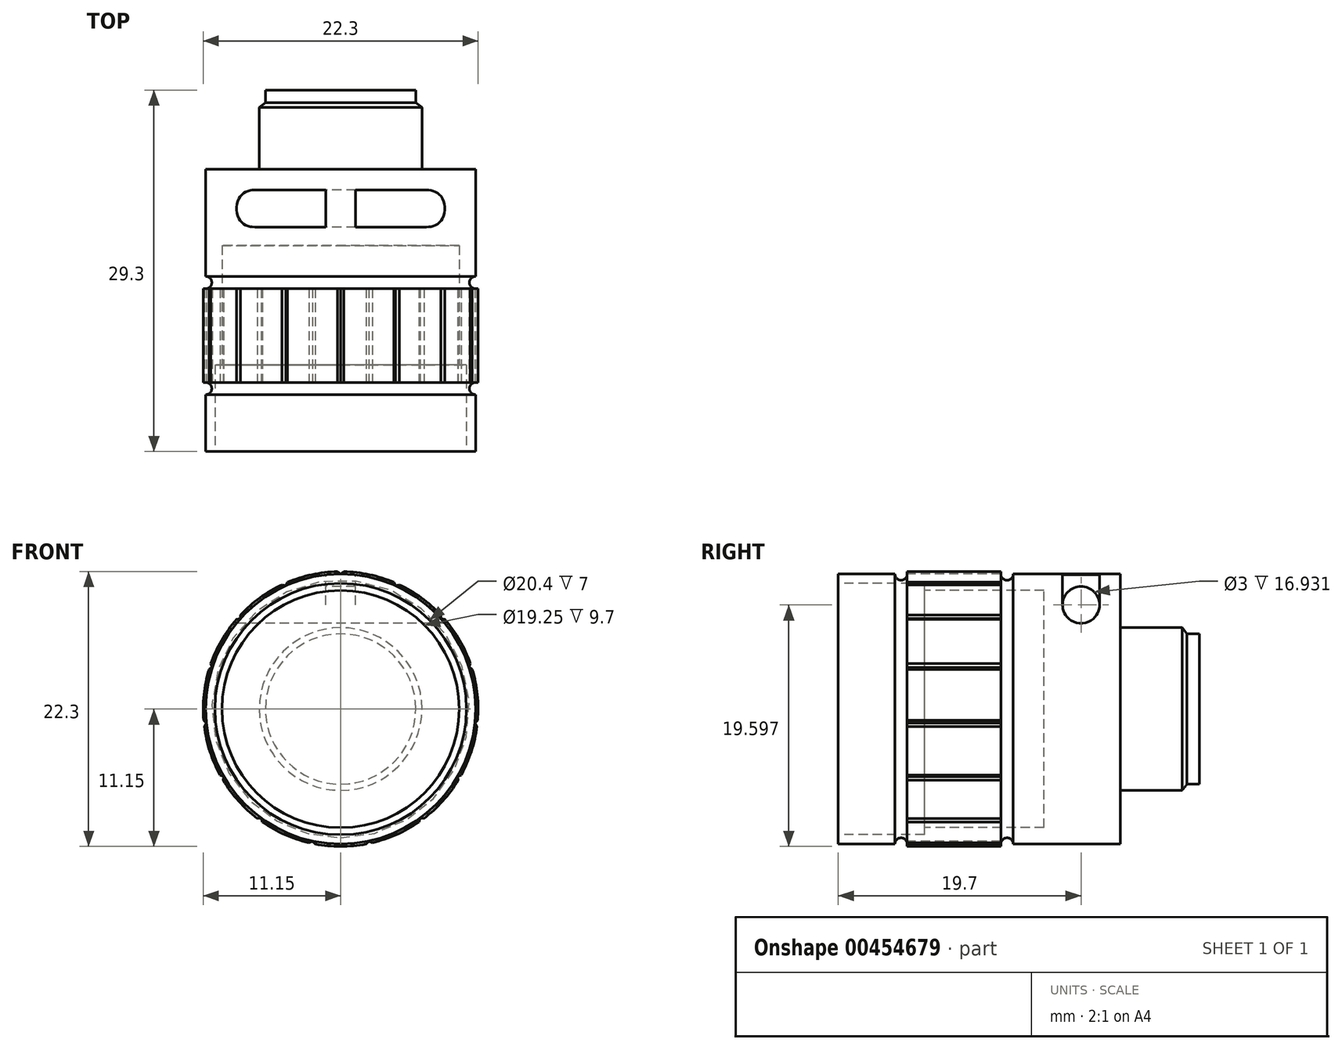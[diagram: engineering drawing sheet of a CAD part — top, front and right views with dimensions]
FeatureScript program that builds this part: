
annotation { "Feature Type Name" : "Feature", "Feature Type Description" : "" }
export const myFeature = defineFeature(function(context is Context, id is Id, definition is map)
    precondition{}
    {
        {
            var Q0;
            Q0=qCreatedBy(makeId("Right.planeOp"),FACE);
            var sketch = newSketch(context, id + "F0", { "sketchPlane" : qUnion([Q0])});
            skLineSegment(sketch, "E0", {"start": v(0, 10.95) * mm, "end": v(0, 10.2) * mm});
            skLineSegment(sketch, "E1", {"start": v(0, 10.2) * mm, "end": v(7, 10.2) * mm});
            skLineSegment(sketch, "E2", {"start": v(7, 10.2) * mm, "end": v(7, 9.63) * mm});
            skLineSegment(sketch, "E3", {"start": v(7, 9.63) * mm, "end": v(16.7, 9.63) * mm});
            skLineSegment(sketch, "E4", {"start": v(16.7, 9.63) * mm, "end": v(16.7, 0) * mm});
            skLineSegment(sketch, "E5", {"start": v(16.7, 0) * mm, "end": v(29.3, 0) * mm});
            skLineSegment(sketch, "E6", {"start": v(29.3, 0) * mm, "end": v(29.3, 6.1) * mm});
            skLineSegment(sketch, "E7", {"start": v(29.3, 6.1) * mm, "end": v(28.3, 6.1) * mm});
            skLineSegment(sketch, "E8", {"start": v(28.3, 6.1) * mm, "end": v(27.9, 6.6) * mm});
            skLineSegment(sketch, "E9", {"start": v(27.9, 6.6) * mm, "end": v(22.9, 6.6) * mm});
            skLineSegment(sketch, "E10", {"start": v(22.9, 6.6) * mm, "end": v(22.9, 10.95) * mm});
            skLineSegment(sketch, "E11", {"start": v(0, 10.95) * mm, "end": v(4.6, 10.95) * mm});
            skArc(sketch, "E12", {"start": v(4.6, 10.95) * mm, "mid": v(5.1, 10.45) * mm, "end": v(5.6, 10.95) * mm});
            skArc(sketch, "E13", {"start": v(13.2, 10.95) * mm, "mid": v(13.7, 10.45) * mm, "end": v(14.2, 10.95) * mm});
            skLineSegment(sketch, "E14", {"start": v(14.2, 10.95) * mm, "end": v(22.9, 10.95) * mm});
            skLineSegment(sketch, "E15", {"start": v(5.6, 10.95) * mm, "end": v(5.6, 11.15) * mm});
            skLineSegment(sketch, "E16", {"start": v(5.6, 11.15) * mm, "end": v(13.2, 11.15) * mm});
            skLineSegment(sketch, "E17", {"start": v(13.2, 10.95) * mm, "end": v(13.2, 11.15) * mm});
            skSolve(sketch);
        }
        {
            var Q0;
            Q0=qCreatedBy(makeId("Right.planeOp"),FACE);
            var sketch = newSketch(context, id + "F1", { "sketchPlane" : qUnion([Q0])});
            skLineSegment(sketch, "E18", {"start": v(-50.3, 0) * mm, "end": v(55.17, 0) * mm, "construction": true});
            skSolve(sketch);
        }
        {
            var Q0;
            Q0=makeQuery(id+"F0.imprint","IMPRINT",FACE,{"disambiguationData":[TD([[makeQuery(id+"F0.imprint","IMPRINT",EDGE,{"derivedFrom":sQuery(id+"F0.wireOp",EDGE,"E0")}),1.0]])]});
            var Q1;
            Q1=sQuery(id+"F1.wireOp",EDGE,"E18");
            revolve(context, id + "F2", {"entities" : qUnion([Q0]), "axis" : qUnion([Q1]), "revolveType" : RevolveType.FULL});
        }
        {
            var Q0;
            Q0=qCreatedBy(makeId("Front.planeOp"),FACE);
            var sketch = newSketch(context, id + "F3", { "sketchPlane" : qUnion([Q0])});
            skLineSegment(sketch, "E19", {"start": v(0.25, 11.6) * mm, "end": v(-0.25, 11.6) * mm, "construction": true});
            skLineSegment(sketch, "E20", {"start": v(0, 10.95) * mm, "end": v(-0.25, 11.15) * mm});
            skLineSegment(sketch, "E21", {"start": v(0, 10.95) * mm, "end": v(0.25, 11.15) * mm});
            skLineSegment(sketch, "E22", {"start": v(-0.25, 11.15) * mm, "end": v(-0.25, 11.25) * mm});
            skLineSegment(sketch, "E23", {"start": v(-0.25, 11.25) * mm, "end": v(0.25, 11.25) * mm});
            skLineSegment(sketch, "E24", {"start": v(0.25, 11.25) * mm, "end": v(0.25, 11.15) * mm});
            skLineSegment(sketch, "E25.1.0", {"start": v(-4.76, 10.08) * mm, "end": v(-4.8, 10.17) * mm});
            skLineSegment(sketch, "E25.1.1", {"start": v(-4.8, 10.17) * mm, "end": v(-4.35, 10.38) * mm});
            skLineSegment(sketch, "E25.1.2", {"start": v(-4.45, 10) * mm, "end": v(-4.76, 10.08) * mm});
            skLineSegment(sketch, "E25.1.3", {"start": v(-4.45, 10) * mm, "end": v(-4.3, 10.29) * mm});
            skLineSegment(sketch, "E25.1.4", {"start": v(-4.35, 10.38) * mm, "end": v(-4.3, 10.29) * mm});
            skLineSegment(sketch, "E25.2.0", {"start": v(-8.45, 7.28) * mm, "end": v(-8.53, 7.34) * mm});
            skLineSegment(sketch, "E25.2.1", {"start": v(-8.53, 7.34) * mm, "end": v(-8.2, 7.71) * mm});
            skLineSegment(sketch, "E25.2.2", {"start": v(-8.14, 7.33) * mm, "end": v(-8.45, 7.28) * mm});
            skLineSegment(sketch, "E25.2.3", {"start": v(-8.14, 7.33) * mm, "end": v(-8.12, 7.65) * mm});
            skLineSegment(sketch, "E25.2.4", {"start": v(-8.2, 7.71) * mm, "end": v(-8.12, 7.65) * mm});
            skLineSegment(sketch, "E25.3.0", {"start": v(-10.68, 3.2) * mm, "end": v(-10.77, 3.24) * mm});
            skLineSegment(sketch, "E25.3.1", {"start": v(-10.77, 3.24) * mm, "end": v(-10.62, 3.71) * mm});
            skLineSegment(sketch, "E25.3.2", {"start": v(-10.41, 3.38) * mm, "end": v(-10.68, 3.2) * mm});
            skLineSegment(sketch, "E25.3.3", {"start": v(-10.41, 3.38) * mm, "end": v(-10.53, 3.68) * mm});
            skLineSegment(sketch, "E25.3.4", {"start": v(-10.62, 3.71) * mm, "end": v(-10.53, 3.68) * mm});
            skLineSegment(sketch, "E25.4.0", {"start": v(-11.06, -1.41) * mm, "end": v(-11.16, -1.42) * mm});
            skLineSegment(sketch, "E25.4.1", {"start": v(-11.16, -1.42) * mm, "end": v(-11.21, -0.93) * mm});
            skLineSegment(sketch, "E25.4.2", {"start": v(-10.9, -1.14) * mm, "end": v(-11.06, -1.41) * mm});
            skLineSegment(sketch, "E25.4.3", {"start": v(-10.9, -1.14) * mm, "end": v(-11.12, -0.92) * mm});
            skLineSegment(sketch, "E25.4.4", {"start": v(-11.21, -0.93) * mm, "end": v(-11.12, -0.92) * mm});
            skLineSegment(sketch, "E25.5.0", {"start": v(-9.53, -5.8) * mm, "end": v(-9.62, -5.84) * mm});
            skLineSegment(sketch, "E25.5.1", {"start": v(-9.62, -5.84) * mm, "end": v(-9.87, -5.4) * mm});
            skLineSegment(sketch, "E25.5.2", {"start": v(-9.48, -5.47) * mm, "end": v(-9.53, -5.8) * mm});
            skLineSegment(sketch, "E25.5.3", {"start": v(-9.48, -5.47) * mm, "end": v(-9.78, -5.36) * mm});
            skLineSegment(sketch, "E25.5.4", {"start": v(-9.87, -5.4) * mm, "end": v(-9.78, -5.36) * mm});
            skLineSegment(sketch, "E25.6.0", {"start": v(-6.35, -9.17) * mm, "end": v(-6.4, -9.25) * mm});
            skLineSegment(sketch, "E25.6.1", {"start": v(-6.4, -9.25) * mm, "end": v(-6.81, -8.95) * mm});
            skLineSegment(sketch, "E25.6.2", {"start": v(-6.44, -8.86) * mm, "end": v(-6.35, -9.17) * mm});
            skLineSegment(sketch, "E25.6.3", {"start": v(-6.44, -8.86) * mm, "end": v(-6.76, -8.87) * mm});
            skLineSegment(sketch, "E25.6.4", {"start": v(-6.81, -8.95) * mm, "end": v(-6.76, -8.87) * mm});
            skLineSegment(sketch, "E25.7.0", {"start": v(-2.07, -10.96) * mm, "end": v(-2.1, -11.05) * mm});
            skLineSegment(sketch, "E25.7.1", {"start": v(-2.1, -11.05) * mm, "end": v(-2.58, -10.95) * mm});
            skLineSegment(sketch, "E25.7.2", {"start": v(-2.28, -10.71) * mm, "end": v(-2.07, -10.96) * mm});
            skLineSegment(sketch, "E25.7.3", {"start": v(-2.28, -10.71) * mm, "end": v(-2.56, -10.85) * mm});
            skLineSegment(sketch, "E25.7.4", {"start": v(-2.58, -10.95) * mm, "end": v(-2.56, -10.85) * mm});
            skLineSegment(sketch, "E25.8.0", {"start": v(2.56, -10.85) * mm, "end": v(2.58, -10.95) * mm});
            skLineSegment(sketch, "E25.8.1", {"start": v(2.58, -10.95) * mm, "end": v(2.1, -11.05) * mm});
            skLineSegment(sketch, "E25.8.2", {"start": v(2.28, -10.71) * mm, "end": v(2.56, -10.85) * mm});
            skLineSegment(sketch, "E25.8.3", {"start": v(2.28, -10.71) * mm, "end": v(2.07, -10.96) * mm});
            skLineSegment(sketch, "E25.8.4", {"start": v(2.1, -11.05) * mm, "end": v(2.07, -10.96) * mm});
            skLineSegment(sketch, "E25.9.0", {"start": v(6.76, -8.87) * mm, "end": v(6.81, -8.95) * mm});
            skLineSegment(sketch, "E25.9.1", {"start": v(6.81, -8.95) * mm, "end": v(6.4, -9.25) * mm});
            skLineSegment(sketch, "E25.9.2", {"start": v(6.44, -8.86) * mm, "end": v(6.76, -8.87) * mm});
            skLineSegment(sketch, "E25.9.3", {"start": v(6.44, -8.86) * mm, "end": v(6.35, -9.17) * mm});
            skLineSegment(sketch, "E25.9.4", {"start": v(6.4, -9.25) * mm, "end": v(6.35, -9.17) * mm});
            skLineSegment(sketch, "E25.10.0", {"start": v(9.78, -5.36) * mm, "end": v(9.87, -5.4) * mm});
            skLineSegment(sketch, "E25.10.1", {"start": v(9.87, -5.4) * mm, "end": v(9.62, -5.84) * mm});
            skLineSegment(sketch, "E25.10.2", {"start": v(9.48, -5.48) * mm, "end": v(9.78, -5.36) * mm});
            skLineSegment(sketch, "E25.10.3", {"start": v(9.48, -5.48) * mm, "end": v(9.53, -5.8) * mm});
            skLineSegment(sketch, "E25.10.4", {"start": v(9.62, -5.84) * mm, "end": v(9.53, -5.8) * mm});
            skLineSegment(sketch, "E25.11.0", {"start": v(11.12, -0.92) * mm, "end": v(11.21, -0.93) * mm});
            skLineSegment(sketch, "E25.11.1", {"start": v(11.21, -0.93) * mm, "end": v(11.16, -1.42) * mm});
            skLineSegment(sketch, "E25.11.2", {"start": v(10.9, -1.14) * mm, "end": v(11.12, -0.92) * mm});
            skLineSegment(sketch, "E25.11.3", {"start": v(10.9, -1.14) * mm, "end": v(11.06, -1.41) * mm});
            skLineSegment(sketch, "E25.11.4", {"start": v(11.16, -1.42) * mm, "end": v(11.06, -1.41) * mm});
            skLineSegment(sketch, "E25.12.0", {"start": v(10.53, 3.68) * mm, "end": v(10.62, 3.71) * mm});
            skLineSegment(sketch, "E25.12.1", {"start": v(10.62, 3.71) * mm, "end": v(10.77, 3.24) * mm});
            skLineSegment(sketch, "E25.12.2", {"start": v(10.41, 3.38) * mm, "end": v(10.53, 3.68) * mm});
            skLineSegment(sketch, "E25.12.3", {"start": v(10.41, 3.38) * mm, "end": v(10.68, 3.2) * mm});
            skLineSegment(sketch, "E25.12.4", {"start": v(10.77, 3.24) * mm, "end": v(10.68, 3.2) * mm});
            skLineSegment(sketch, "E25.13.0", {"start": v(8.12, 7.65) * mm, "end": v(8.2, 7.71) * mm});
            skLineSegment(sketch, "E25.13.1", {"start": v(8.2, 7.71) * mm, "end": v(8.53, 7.34) * mm});
            skLineSegment(sketch, "E25.13.2", {"start": v(8.14, 7.33) * mm, "end": v(8.12, 7.65) * mm});
            skLineSegment(sketch, "E25.13.3", {"start": v(8.14, 7.33) * mm, "end": v(8.45, 7.28) * mm});
            skLineSegment(sketch, "E25.13.4", {"start": v(8.53, 7.34) * mm, "end": v(8.45, 7.28) * mm});
            skLineSegment(sketch, "E25.14.0", {"start": v(4.3, 10.29) * mm, "end": v(4.35, 10.38) * mm});
            skLineSegment(sketch, "E25.14.1", {"start": v(4.35, 10.38) * mm, "end": v(4.8, 10.17) * mm});
            skLineSegment(sketch, "E25.14.2", {"start": v(4.45, 10) * mm, "end": v(4.3, 10.29) * mm});
            skLineSegment(sketch, "E25.14.3", {"start": v(4.45, 10) * mm, "end": v(4.76, 10.08) * mm});
            skLineSegment(sketch, "E25.14.4", {"start": v(4.8, 10.17) * mm, "end": v(4.76, 10.08) * mm});
            skPoint(sketch, "E25.center", {"position": v(0, 0) * mm});
            skSolve(sketch);
        }
        {
            var Q0;
            Q0 = qSketchRegion(id + "F3", true);
            extrude(context, id + "F4", {"entities" : qUnion([Q0]), "operationType" : NewBodyOperationType.REMOVE, "oppositeDirection" : true, "depth" : 25 * mm});
        }
        {
            var Q0;
            Q0=qCreatedBy(makeId("Right.planeOp"),FACE);
            var sketch = newSketch(context, id + "F5", { "sketchPlane" : qUnion([Q0])});
            skCircle(sketch, "E26", {"center": v(19.7, 8.45) * mm, "radius": 1.5 * mm});
            skSolve(sketch);
        }
        {
            var Q0;
            Q0 = qSketchRegion(id + "F5", true);
            var Q1;
            Q1=sQuery(id+"F5.wireOp",EDGE,"E26");
            extrude(context, id + "F6", {"entities" : qUnion([Q0]), "operationType" : NewBodyOperationType.REMOVE, "surfaceEntities" : qUnion([Q1]), "endBound" : BoundingType.SYMMETRIC, "depth" : 25 * mm});
        }
        {
            var Q0;
            Q0=qCreatedBy(makeId("Top.planeOp"),FACE);
            cPlane(context, id + "F7", {"entities" : qUnion([Q0]), "cplaneType" : CPlaneType.OFFSET, "offset" : 11.15 * mm, "width" : 150 * mm, "height" : 150 * mm});
        }
        {
            var Q0;
            Q0=qCreatedBy(id+"F7.planeOp",FACE);
            var sketch = newSketch(context, id + "F8", { "sketchPlane" : qUnion([Q0])});
            skLineSegment(sketch, "E27.bottom", {"start": v(-11.2, 21.2) * mm, "end": v(-1.2, 21.2) * mm});
            skLineSegment(sketch, "E27.top", {"start": v(-11.2, 18.2) * mm, "end": v(-1.2, 18.2) * mm});
            skLineSegment(sketch, "E27.left", {"start": v(-11.2, 21.2) * mm, "end": v(-11.2, 18.2) * mm});
            skLineSegment(sketch, "E27.right", {"start": v(-1.2, 21.2) * mm, "end": v(-1.2, 18.2) * mm});
            skLineSegment(sketch, "E28.bottom", {"start": v(1.2, 21.2) * mm, "end": v(11.2, 21.2) * mm});
            skLineSegment(sketch, "E28.top", {"start": v(1.2, 18.2) * mm, "end": v(11.2, 18.2) * mm});
            skLineSegment(sketch, "E28.left", {"start": v(1.2, 21.2) * mm, "end": v(1.2, 18.2) * mm});
            skLineSegment(sketch, "E28.right", {"start": v(11.2, 21.2) * mm, "end": v(11.2, 18.2) * mm});
            skSolve(sketch);
        }
        {
            var Q0;
            Q0=makeQuery(id+"F8.imprint","IMPRINT",FACE,{"disambiguationData":[TD([[makeQuery(id+"F8.imprint","IMPRINT",EDGE,{"derivedFrom":sQuery(id+"F8.wireOp",EDGE,"E28.bottom")}),-1.0]])]});
            var Q1;
            Q1=makeQuery(id+"F8.imprint","IMPRINT",FACE,{"disambiguationData":[TD([[makeQuery(id+"F8.imprint","IMPRINT",EDGE,{"derivedFrom":sQuery(id+"F8.wireOp",EDGE,"E27.bottom")}),-1.0]])]});
            extrude(context, id + "F9", {"entities" : qUnion([Q0, Q1]), "operationType" : NewBodyOperationType.REMOVE, "oppositeDirection" : true, "depth" : 2.7 * mm});
        }
    });
